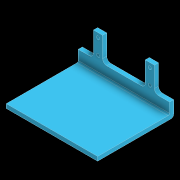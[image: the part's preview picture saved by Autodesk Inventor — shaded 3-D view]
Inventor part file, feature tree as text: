
AUTODESK INVENTOR PART (.ipt)
format: ipt  version: 2020 (Build 240168000, 168)  size: 178,688 bytes
history: native  units: mm
features: extrude x5, sketch x5, other x4, fillet x3
ambient origin geometry x8: Origin, YZ Plane, XZ Plane, XY Plane, X Axis, Y Axis, Z Axis, Center Point
bodies: Body1 (feature_tree)
feature tree (17):
  other  "實體1"
  extrude  "擠出1"  Depth=33.0mm
  extrude  "擠出2"  Depth=33.0mm
  extrude  "擠出3"  Depth=220.0mm
  extrude  "擠出4"  Depth=110.0mm
  extrude  "擠出5"  Depth=88.0mm
  fillet  "圓角1"  Radius=88.0mm
  fillet  "圓角2"  Radius=55.0mm
  fillet  "圓角3"  Radius=55.0mm
  sketch  "草圖1"
  sketch  "草圖2"
  sketch  "草圖3"
  sketch  "草圖4"
  sketch  "草圖5"
  other  "投影切割邊1"
  other  "投影切割邊2"
  other  "投影切割邊3"
